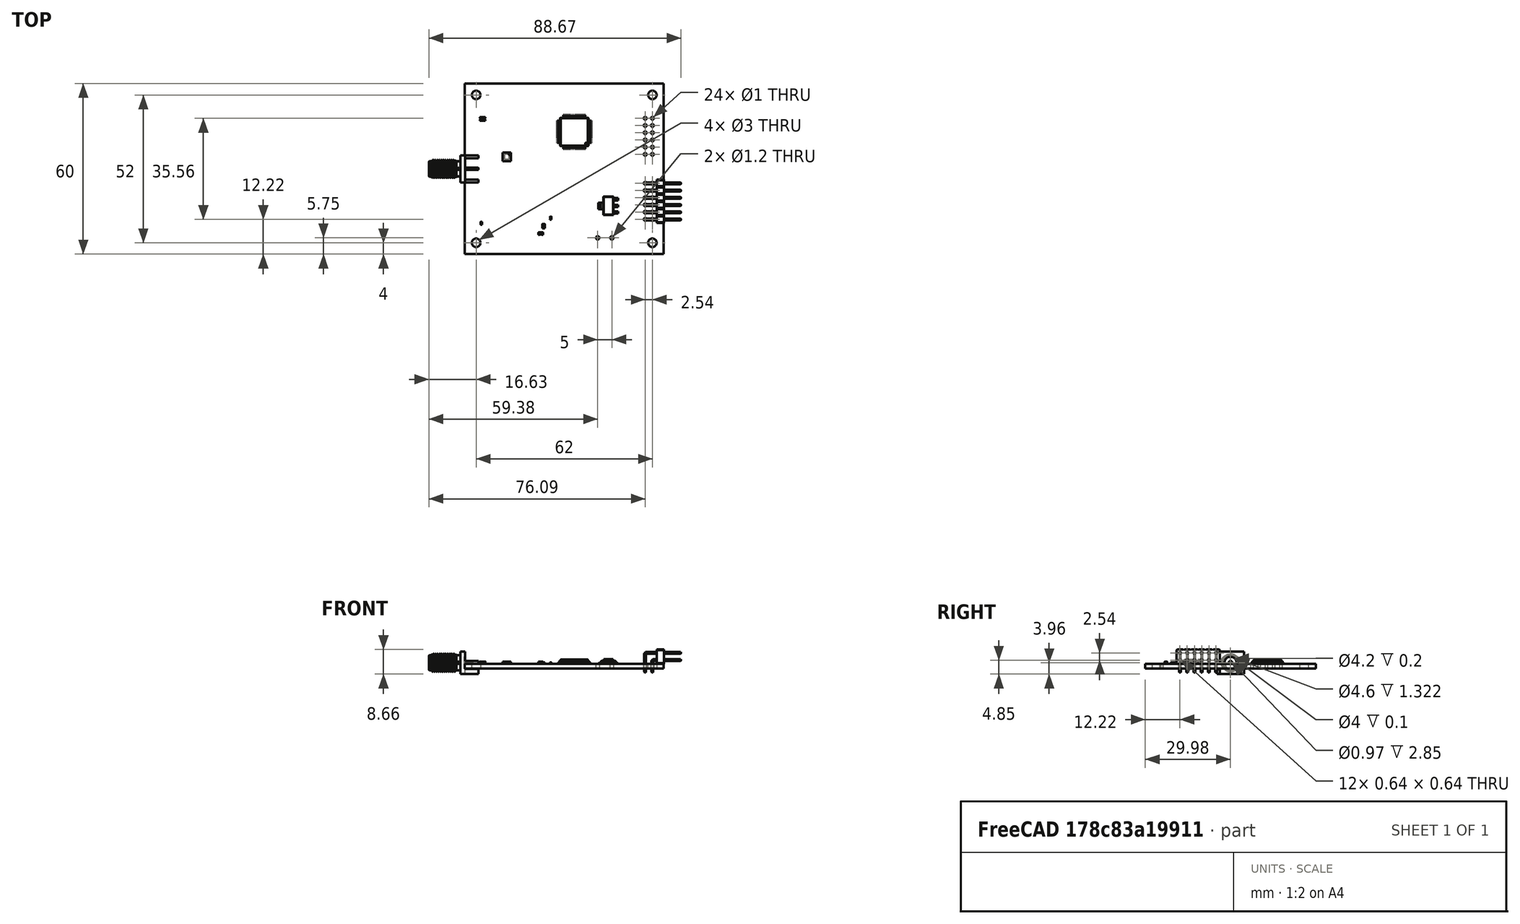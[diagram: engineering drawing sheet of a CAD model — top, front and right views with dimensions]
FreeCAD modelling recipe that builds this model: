
FCSTD DOCUMENT  (FreeCAD 1.0R39109 (Git))
Label: SixPort120_BDv2_12GHz
License: All rights reserved
LicenseURL: https://en.wikipedia.org/wiki/All_rights_reserved
objects: App::Link×60, Part::Feature×11, App::Part×4, PartDesign::CoordinateSystem×1, Sketcher::SketchObject×1
note: 14 computed .brp shape members not serialized (recipe doc carries the construction recipe); baked Part::Feature solids carry a one-line shape summary decoded from their .brp

FEATURE [PartDesign::CoordinateSystem] Local_CS_4f05
  AttacherType = Attacher::AttachEngine3D
  MapMode = 2
FEATURE [Part::Feature] Pcb_4f05
  Placement = pos=(-141,119.75,0) rot=(0,0,1;0rad)
  shape: bbox 70 x 60 x 1.6 mm, 36 faces (baked)
FEATURE [Sketcher::SketchObject] PCB_Sketch_4f05
  ArcFitTolerance = 1e-06
  FullyConstrained = false
  MakeInternals = false
  sketch-geometry (4):
    g0: LineSegment StartX=66 StartY=-4 StartZ=0 EndX=-4 EndY=-4 EndZ=0
    g1: LineSegment StartX=66 StartY=56 StartZ=0 EndX=66 EndY=-4 EndZ=0
    g2: LineSegment StartX=-4 StartY=56 StartZ=0 EndX=66 EndY=56 EndZ=0
    g3: LineSegment StartX=-4 StartY=-4 StartZ=0 EndX=-4 EndY=56 EndZ=0
  constraints (4):
    c: Coincident(g0,g3)
    c: Coincident(g2,g3)
    c: Coincident(g0,g1)
    c: Coincident(g1,g2)
FEATURE [App::Part] Board_Geoms_4f05
  Group = -> [Pcb_4f05,PCB_Sketch_4f05]
  Origin = -> Origin
FEATURE [Part::Feature] Shape  label="C2_1_C_0603_1608Metric_000061b49daf"
  Placement = pos=(22.7,3.25,0) rot=(0,0,1;3.14159rad)
  shape: bbox 1.6 x 0.8 x 0.8 mm, 28 faces (baked)
FEATURE [App::Link] C2_1_C_0603_1608Metric_000061b49daf_ln_  label="C2_2_1_C_0603_1608Metric_000061b49dc0"
  LinkPlacement = pos=(26,3.15,0) rot=(0,0,1;0rad)
  LinkedObject = -> Shape
  Placement = pos=(26,3.15,0) rot=(0,0,1;0rad)
FEATURE [App::Link] C2_1_C_0603_1608Metric_000061b49daf_ln_001  label="C2_3_1_C_0603_1608Metric_000061b49dd1"
  LinkPlacement = pos=(21.9,5.85,0) rot=(0,0,-1;1.5708rad)
  LinkedObject = -> Shape
  Placement = pos=(21.9,5.85,0) rot=(0,0,-1;1.5708rad)
FEATURE [Part::Feature] Shape001  label="C2_4_C_0402_1005Metric_000061b49de2"
  Placement = pos=(26.25,8.675,0) rot=(0,0,1;1.5708rad)
  shape: bbox 0.5 x 1 x 0.5 mm, 28 faces (baked)
FEATURE [App::Link] C2_4_C_0402_1005Metric_000061b49de2_ln_  label="C3_4_4_C_0402_1005Metric_000061b49df3"
  LinkPlacement = pos=(32.9,18.4,0) rot=(0,0,1;3.14159rad)
  LinkedObject = -> Shape001
  Placement = pos=(32.9,18.4,0) rot=(0,0,1;3.14159rad)
FEATURE [App::Link] C2_1_C_0603_1608Metric_000061b49daf_ln_002  label="C3_1_1_C_0603_1608Metric_000061b49e04"
  LinkPlacement = pos=(38.325,14.85,0) rot=(0,0,-1;1.5708rad)
  LinkedObject = -> Shape
  Placement = pos=(38.325,14.85,0) rot=(0,0,-1;1.5708rad)
FEATURE [App::Link] C2_1_C_0603_1608Metric_000061b49daf_ln_003  label="C3_2_1_C_0603_1608Metric_000061b49e15"
  LinkPlacement = pos=(38.425,18.15,0) rot=(0,0,1;1.5708rad)
  LinkedObject = -> Shape
  Placement = pos=(38.425,18.15,0) rot=(0,0,1;1.5708rad)
FEATURE [App::Link] C2_1_C_0603_1608Metric_000061b49daf_ln_004  label="C3_3_1_C_0603_1608Metric_000061b49e26"
  LinkPlacement = pos=(35.725,14.05,0) rot=(0,0,1;0rad)
  LinkedObject = -> Shape
  Placement = pos=(35.725,14.05,0) rot=(0,0,1;0rad)
FEATURE [App::Link] C2_1_C_0603_1608Metric_000061b49daf_ln_005  label="C4_1_1_C_0603_1608Metric_000061b49e37"
  LinkPlacement = pos=(33.7,29.8,0) rot=(0,0,1;0rad)
  LinkedObject = -> Shape
  Placement = pos=(33.7,29.8,0) rot=(0,0,1;0rad)
FEATURE [App::Link] C2_1_C_0603_1608Metric_000061b49daf_ln_006  label="C4_2_1_C_0603_1608Metric_000061b49e48"
  LinkPlacement = pos=(30.4,29.9,0) rot=(0,0,1;3.14159rad)
  LinkedObject = -> Shape
  Placement = pos=(30.4,29.9,0) rot=(0,0,1;3.14159rad)
FEATURE [App::Link] C2_1_C_0603_1608Metric_000061b49daf_ln_007  label="C4_3_1_C_0603_1608Metric_000061b49e59"
  LinkPlacement = pos=(34.6,27,0) rot=(0,0,1;1.5708rad)
  LinkedObject = -> Shape
  Placement = pos=(34.6,27,0) rot=(0,0,1;1.5708rad)
FEATURE [App::Link] C2_4_C_0402_1005Metric_000061b49de2_ln_001  label="C4_4_4_C_0402_1005Metric_000061b49e6a"
  LinkPlacement = pos=(30.15,24.38,0) rot=(0,0,-1;1.5708rad)
  LinkedObject = -> Shape001
  Placement = pos=(30.15,24.38,0) rot=(0,0,-1;1.5708rad)
FEATURE [App::Link] C2_1_C_0603_1608Metric_000061b49daf_ln_008  label="C5_1_1_C_0603_1608Metric_000061b49e7b"
  LinkPlacement = pos=(10.3,0.25,0) rot=(0,0,1;3.14159rad)
  LinkedObject = -> Shape
  Placement = pos=(10.3,0.25,0) rot=(0,0,1;3.14159rad)
FEATURE [App::Link] C2_1_C_0603_1608Metric_000061b49daf_ln_009  label="C5_2_1_C_0603_1608Metric_000061b49e8c"
  LinkPlacement = pos=(13.6,0.15,0) rot=(0,0,1;0rad)
  LinkedObject = -> Shape
  Placement = pos=(13.6,0.15,0) rot=(0,0,1;0rad)
FEATURE [App::Link] C2_1_C_0603_1608Metric_000061b49daf_ln_010  label="C5_3_1_C_0603_1608Metric_000061b49e9d"
  LinkPlacement = pos=(9.3,2.85,0) rot=(0,0,-1;1.5708rad)
  LinkedObject = -> Shape
  Placement = pos=(9.3,2.85,0) rot=(0,0,-1;1.5708rad)
FEATURE [App::Link] C2_4_C_0402_1005Metric_000061b49de2_ln_002  label="C5_4_4_C_0402_1005Metric_000061b49eae"
  LinkPlacement = pos=(13.75,5.675,0) rot=(0,0,1;1.5708rad)
  LinkedObject = -> Shape001
  Placement = pos=(13.75,5.675,0) rot=(0,0,1;1.5708rad)
FEATURE [Part::Feature] Shape002  label="R2_1_R_0603_1608Metric_000061b4a0a3"
  Placement = pos=(23.7,5.825,0) rot=(0,0,-1;1.5708rad)
  shape: bbox 0.8 x 1.6 x 0.45 mm, 26 faces (baked)
FEATURE [App::Link] R2_1_R_0603_1608Metric_000061b4a0a3_ln_  label="R3_1_1_R_0603_1608Metric_000061b4a0b4"
  LinkPlacement = pos=(35.725,15.85,0) rot=(0,0,1;0rad)
  LinkedObject = -> Shape002
  Placement = pos=(35.725,15.85,0) rot=(0,0,1;0rad)
FEATURE [App::Link] R2_1_R_0603_1608Metric_000061b4a0a3_ln_001  label="R4_1_1_R_0603_1608Metric_000061b4a0c5"
  LinkPlacement = pos=(32.7,27,0) rot=(0,0,1;1.5708rad)
  LinkedObject = -> Shape002
  Placement = pos=(32.7,27,0) rot=(0,0,1;1.5708rad)
FEATURE [App::Link] R2_1_R_0603_1608Metric_000061b4a0a3_ln_002  label="R5_1_1_R_0603_1608Metric_000061b4a0d6"
  LinkPlacement = pos=(11.1,2.85,0) rot=(0,0,-1;1.5708rad)
  LinkedObject = -> Shape002
  Placement = pos=(11.1,2.85,0) rot=(0,0,-1;1.5708rad)
FEATURE [Part::Feature] Shape003  label="R0_3_R_0402_1005Metric_000063accc0d"
  Placement = pos=(1.75,6.84,0) rot=(0,0,-1;1.5708rad)
  shape: bbox 0.5 x 1 x 0.35 mm, 26 faces (baked)
FEATURE [App::Link] R0_3_R_0402_1005Metric_000063accc0d_ln_  label="R0_2_3_R_0402_1005Metric_000063accc3d"
  LinkPlacement = pos=(9.48,10.29,0) rot=(0,0,1;3.14159rad)
  LinkedObject = -> Shape003
  Placement = pos=(9.48,10.29,0) rot=(0,0,1;3.14159rad)
FEATURE [App::Link] R0_3_R_0402_1005Metric_000063accc0d_ln_001  label="R0_1_3_R_0402_1005Metric_000063acccbe"
  LinkPlacement = pos=(9.48,18.4,0) rot=(0,0,1;3.14159rad)
  LinkedObject = -> Shape003
  Placement = pos=(9.48,18.4,0) rot=(0,0,1;3.14159rad)
FEATURE [App::Link] R0_3_R_0402_1005Metric_000063accc0d_ln_002  label="R0_4_3_R_0402_1005Metric_000063ad1704"
  LinkPlacement = pos=(5.54,6.84,0) rot=(0,0,-1;1.5708rad)
  LinkedObject = -> Shape003
  Placement = pos=(5.54,6.84,0) rot=(0,0,-1;1.5708rad)
FEATURE [App::Link] C2_1_C_0603_1608Metric_000061b49daf_ln_011  label="C7_1_1_C_0603_1608Metric_000063cef614"
  LinkPlacement = pos=(14.25,29.25,0) rot=(0,0,1;1.5708rad)
  LinkedObject = -> Shape
  Placement = pos=(14.25,29.25,0) rot=(0,0,1;1.5708rad)
FEATURE [App::Link] C2_1_C_0603_1608Metric_000061b49daf_ln_012  label="C7_3_1_C_0603_1608Metric_000063cef636"
  LinkPlacement = pos=(18.75,29.25,0) rot=(0,0,1;1.5708rad)
  LinkedObject = -> Shape
  Placement = pos=(18.75,29.25,0) rot=(0,0,1;1.5708rad)
FEATURE [App::Link] C2_1_C_0603_1608Metric_000061b49daf_ln_013  label="C7_4_1_C_0603_1608Metric_000063cef647"
  LinkPlacement = pos=(14.25,32.5,0) rot=(0,0,-1;1.5708rad)
  LinkedObject = -> Shape
  Placement = pos=(14.25,32.5,0) rot=(0,0,-1;1.5708rad)
FEATURE [App::Link] C2_1_C_0603_1608Metric_000061b49daf_ln_014  label="C7_5_1_C_0603_1608Metric_000063cef658"
  LinkPlacement = pos=(16.5,32.5,0) rot=(0,0,-1;1.5708rad)
  LinkedObject = -> Shape
  Placement = pos=(16.5,32.5,0) rot=(0,0,-1;1.5708rad)
FEATURE [App::Link] C2_1_C_0603_1608Metric_000061b49daf_ln_015  label="C7_6_1_C_0603_1608Metric_000063cef669"
  LinkPlacement = pos=(18.75,32.5,0) rot=(0,0,-1;1.5708rad)
  LinkedObject = -> Shape
  Placement = pos=(18.75,32.5,0) rot=(0,0,-1;1.5708rad)
FEATURE [App::Link] C2_1_C_0603_1608Metric_000061b49daf_ln_016  label="C8_1_1_C_0603_1608Metric_000063cef67a"
  LinkPlacement = pos=(46.5,8.25,0) rot=(0,0,1;0rad)
  LinkedObject = -> Shape
  Placement = pos=(46.5,8.25,0) rot=(0,0,1;0rad)
FEATURE [App::Link] C2_1_C_0603_1608Metric_000061b49daf_ln_017  label="C8_2_1_C_0603_1608Metric_000063cef68b"
  LinkPlacement = pos=(46.5,17.75,0) rot=(0,0,1;0rad)
  LinkedObject = -> Shape
  Placement = pos=(46.5,17.75,0) rot=(0,0,1;0rad)
FEATURE [App::Link] C2_1_C_0603_1608Metric_000061b49daf_ln_018  label="C8_3_1_C_0603_1608Metric_000063cef69c"
  LinkPlacement = pos=(46.5,20.5,0) rot=(0,0,1;0rad)
  LinkedObject = -> Shape
  Placement = pos=(46.5,20.5,0) rot=(0,0,1;0rad)
FEATURE [App::Link] C2_1_C_0603_1608Metric_000061b49daf_ln_019  label="C8_4_1_C_0603_1608Metric_000063cef6ad"
  LinkPlacement = pos=(47.25,30,0) rot=(0,0,1;0rad)
  LinkedObject = -> Shape
  Placement = pos=(47.25,30,0) rot=(0,0,1;0rad)
FEATURE [Part::Feature] Shape004  label="U7_1_QFN-12-1EP_3x3mm_Pitch0.5mm_000063cefc6c"
  Placement = pos=(10.75,30.25,0) rot=(0,0,-1;1.5708rad)
  shape: bbox 3 x 3 x 0.77 mm, 86 faces (baked)
FEATURE [Part::Feature] Shape005  label="U8_1_SOT_223_000063cefc82"
  Placement = pos=(46.5,13,0) rot=(0,0,1;3.14159rad)
  shape: bbox 7 x 6.5 x 1.7 mm, 78 faces (baked)
FEATURE [App::Link] U8_1_SOT_223_000063cefc82_ln_  label="U8_2_1_SOT_223_000063cefc98"
  LinkPlacement = pos=(46.5,25.25,0) rot=(0,0,1;3.14159rad)
  LinkedObject = -> Shape005
  Placement = pos=(46.5,25.25,0) rot=(0,0,1;3.14159rad)
FEATURE [App::Link] C2_1_C_0603_1608Metric_000061b49daf_ln_020  label="C7_2_1_C_0603_1608Metric_000063cf222f"
  LinkPlacement = pos=(16.5,29.25,0) rot=(0,0,1;1.5708rad)
  LinkedObject = -> Shape
  Placement = pos=(16.5,29.25,0) rot=(0,0,1;1.5708rad)
FEATURE [App::Link] C2_1_C_0603_1608Metric_000061b49daf_ln_021  label="C1_2_1_C_0603_1608Metric_000063d513af"
  LinkPlacement = pos=(11.5,44.75,0) rot=(0,0,1;1.5708rad)
  LinkedObject = -> Shape
  Placement = pos=(11.5,44.75,0) rot=(0,0,1;1.5708rad)
FEATURE [App::Link] C2_1_C_0603_1608Metric_000061b49daf_ln_022  label="C1_1_1_C_0603_1608Metric_000063d513bf"
  LinkPlacement = pos=(5.5,44.75,0) rot=(0,0,-1;1.5708rad)
  LinkedObject = -> Shape
  Placement = pos=(5.5,44.75,0) rot=(0,0,-1;1.5708rad)
FEATURE [App::Link] C2_1_C_0603_1608Metric_000061b49daf_ln_023  label="C1_15_1_C_0603_1608Metric_000063d513cf"
  LinkPlacement = pos=(16,37,0) rot=(0,0,1;0rad)
  LinkedObject = -> Shape
  Placement = pos=(16,37,0) rot=(0,0,1;0rad)
FEATURE [App::Link] C2_1_C_0603_1608Metric_000061b49daf_ln_024  label="C1_11_1_C_0603_1608Metric_000063d513df"
  LinkPlacement = pos=(15,44.75,0) rot=(0,0,1;1.5708rad)
  LinkedObject = -> Shape
  Placement = pos=(15,44.75,0) rot=(0,0,1;1.5708rad)
FEATURE [App::Link] C2_1_C_0603_1608Metric_000061b49daf_ln_025  label="C1_13_1_C_0603_1608Metric_000063d513ef"
  LinkPlacement = pos=(3.5,33.25,0) rot=(0,0,1;3.14159rad)
  LinkedObject = -> Shape
  Placement = pos=(3.5,33.25,0) rot=(0,0,1;3.14159rad)
FEATURE [App::Link] C2_1_C_0603_1608Metric_000061b49daf_ln_026  label="C1_9_1_C_0603_1608Metric_000063d513ff"
  LinkPlacement = pos=(16.75,44.75,0) rot=(0,0,1;1.5708rad)
  LinkedObject = -> Shape
  Placement = pos=(16.75,44.75,0) rot=(0,0,1;1.5708rad)
FEATURE [App::Link] C2_1_C_0603_1608Metric_000061b49daf_ln_027  label="C1_8_1_C_0603_1608Metric_000063d5140f"
  LinkPlacement = pos=(16,42.25,0) rot=(0,0,1;0rad)
  LinkedObject = -> Shape
  Placement = pos=(16,42.25,0) rot=(0,0,1;0rad)
FEATURE [App::Link] C2_1_C_0603_1608Metric_000061b49daf_ln_028  label="C1_10_1_C_0603_1608Metric_000063d5141f"
  LinkPlacement = pos=(13.25,44.75,0) rot=(0,0,1;1.5708rad)
  LinkedObject = -> Shape
  Placement = pos=(13.25,44.75,0) rot=(0,0,1;1.5708rad)
FEATURE [App::Link] C2_1_C_0603_1608Metric_000061b49daf_ln_029  label="C1_5_1_C_0603_1608Metric_000063d5144f"
  LinkPlacement = pos=(3.5,35,0) rot=(0,0,1;3.14159rad)
  LinkedObject = -> Shape
  Placement = pos=(3.5,35,0) rot=(0,0,1;3.14159rad)
FEATURE [App::Link] C2_1_C_0603_1608Metric_000061b49daf_ln_030  label="C1_3_1_C_0603_1608Metric_000063d5145f"
  LinkPlacement = pos=(3.5,41.5,0) rot=(0,0,1;3.14159rad)
  LinkedObject = -> Shape
  Placement = pos=(3.5,41.5,0) rot=(0,0,1;3.14159rad)
FEATURE [App::Link] C2_1_C_0603_1608Metric_000061b49daf_ln_031  label="C1_14_1_C_0603_1608Metric_000063d5146f"
  LinkPlacement = pos=(3.5,31.5,0) rot=(0,0,1;3.14159rad)
  LinkedObject = -> Shape
  Placement = pos=(3.5,31.5,0) rot=(0,0,1;3.14159rad)
FEATURE [App::Link] C2_1_C_0603_1608Metric_000061b49daf_ln_032  label="C1_4_1_C_0603_1608Metric_000063d5147f"
  LinkPlacement = pos=(3.5,38.5,0) rot=(0,0,1;3.14159rad)
  LinkedObject = -> Shape
  Placement = pos=(3.5,38.5,0) rot=(0,0,1;3.14159rad)
FEATURE [App::Link] C2_4_C_0402_1005Metric_000061b49de2_ln_003  label="C1_12_4_C_0402_1005Metric_000063d514e4"
  LinkPlacement = pos=(10.75,34.15,0) rot=(0,0,1;1.5708rad)
  LinkedObject = -> Shape001
  Placement = pos=(10.75,34.15,0) rot=(0,0,1;1.5708rad)
FEATURE [App::Link] R2_1_R_0603_1608Metric_000061b4a0a3_ln_003  label="R1_3_1_R_0603_1608Metric_000063d51504"
  LinkPlacement = pos=(1,32.25,0) rot=(0,0,1;1.5708rad)
  LinkedObject = -> Shape002
  Placement = pos=(1,32.25,0) rot=(0,0,1;1.5708rad)
FEATURE [Part::Feature] Shape006  label="D1_1_D_0805_000063d51534"
  Placement = pos=(2.25,43.5,0) rot=(0,0,1;3.14159rad)
  shape: bbox 2 x 1.27 x 0.8 mm, 39 faces (baked)
FEATURE [App::Link] R2_1_R_0603_1608Metric_000061b4a0a3_ln_004  label="R1_1_1_R_0603_1608Metric_000063d5338b"
  LinkPlacement = pos=(2.75,45.5,0) rot=(0,0,1;0rad)
  LinkedObject = -> Shape002
  Placement = pos=(2.75,45.5,0) rot=(0,0,1;0rad)
FEATURE [App::Link] R2_1_R_0603_1608Metric_000061b4a0a3_ln_005  label="R1_5_1_R_0603_1608Metric_000063d53636"
  LinkPlacement = pos=(16,40.5,0) rot=(0,0,1;0rad)
  LinkedObject = -> Shape002
  Placement = pos=(16,40.5,0) rot=(0,0,1;0rad)
FEATURE [App::Link] R2_1_R_0603_1608Metric_000061b4a0a3_ln_006  label="R1_2_1_R_0603_1608Metric_000063d54fa1"
  LinkPlacement = pos=(16,38.75,0) rot=(0,0,1;3.14159rad)
  LinkedObject = -> Shape002
  Placement = pos=(16,38.75,0) rot=(0,0,1;3.14159rad)
FEATURE [App::Link] C2_1_C_0603_1608Metric_000061b49daf_ln_033  label="C1_6_1_C_0603_1608Metric_000063d56b6d"
  LinkPlacement = pos=(19.25,35,0) rot=(0,0,1;0rad)
  LinkedObject = -> Shape
  Placement = pos=(19.25,35,0) rot=(0,0,1;0rad)
FEATURE [App::Link] C2_1_C_0603_1608Metric_000061b49daf_ln_034  label="C1_7_1_C_0603_1608Metric_000063d56b9f"
  LinkPlacement = pos=(16,35,0) rot=(0,0,1;3.14159rad)
  LinkedObject = -> Shape
  Placement = pos=(16,35,0) rot=(0,0,1;3.14159rad)
FEATURE [App::Link] C2_1_C_0603_1608Metric_000061b49daf_ln_035  label="C6_2_1_C_0603_1608Metric_000063d66c4c"
  LinkPlacement = pos=(25.25,40.75,0) rot=(0,0,1;3.14159rad)
  LinkedObject = -> Shape
  Placement = pos=(25.25,40.75,0) rot=(0,0,1;3.14159rad)
FEATURE [App::Link] C2_1_C_0603_1608Metric_000061b49daf_ln_036  label="C6_9_1_C_0603_1608Metric_000063d66c5c"
  LinkPlacement = pos=(25.25,44.25,0) rot=(0,0,1;3.14159rad)
  LinkedObject = -> Shape
  Placement = pos=(25.25,44.25,0) rot=(0,0,1;3.14159rad)
FEATURE [App::Link] C2_1_C_0603_1608Metric_000061b49daf_ln_037  label="C6_5_1_C_0603_1608Metric_000063d66c6c"
  LinkPlacement = pos=(25.25,42.5,0) rot=(0,0,1;3.14159rad)
  LinkedObject = -> Shape
  Placement = pos=(25.25,42.5,0) rot=(0,0,1;3.14159rad)
FEATURE [App::Link] C2_1_C_0603_1608Metric_000061b49daf_ln_038  label="C6_4_1_C_0603_1608Metric_000063d66c7c"
  LinkPlacement = pos=(25.25,37.25,0) rot=(0,0,1;3.14159rad)
  LinkedObject = -> Shape
  Placement = pos=(25.25,37.25,0) rot=(0,0,1;3.14159rad)
FEATURE [App::Link] C2_1_C_0603_1608Metric_000061b49daf_ln_039  label="C6_8_1_C_0603_1608Metric_000063d66c8c"
  LinkPlacement = pos=(42.5,37.5,0) rot=(0,0,-1;1.5708rad)
  LinkedObject = -> Shape
  Placement = pos=(42.5,37.5,0) rot=(0,0,-1;1.5708rad)
FEATURE [App::Link] C2_1_C_0603_1608Metric_000061b49daf_ln_040  label="C6_6_1_C_0603_1608Metric_000063d66c9c"
  LinkPlacement = pos=(25.25,39,0) rot=(0,0,1;3.14159rad)
  LinkedObject = -> Shape
  Placement = pos=(25.25,39,0) rot=(0,0,1;3.14159rad)
FEATURE [Part::Feature] Shape007  label="U6_1_LQFP_64_10x10mm_P05mm_000063d66cac"
  Placement = pos=(34.5,39,0) rot=(0,0,1;3.14159rad)
  shape: bbox 12 x 12 x 1.5 mm, 1004 faces (baked)
FEATURE [App::Link] C2_1_C_0603_1608Metric_000061b49daf_ln_041  label="C6_7_1_C_0603_1608Metric_000063d66d16"
  LinkPlacement = pos=(25.25,35.5,0) rot=(0,0,1;3.14159rad)
  LinkedObject = -> Shape
  Placement = pos=(25.25,35.5,0) rot=(0,0,1;3.14159rad)
FEATURE [App::Link] C2_1_C_0603_1608Metric_000061b49daf_ln_042  label="C6_3_1_C_0603_1608Metric_000063d66d26"
  LinkPlacement = pos=(25.25,33.75,0) rot=(0,0,1;3.14159rad)
  LinkedObject = -> Shape
  Placement = pos=(25.25,33.75,0) rot=(0,0,1;3.14159rad)
FEATURE [App::Link] C2_1_C_0603_1608Metric_000061b49daf_ln_043  label="C6_1_1_C_0603_1608Metric_000063d66d87"
  LinkPlacement = pos=(42.5,34.3,0) rot=(0,0,-1;1.5708rad)
  LinkedObject = -> Shape
  Placement = pos=(42.5,34.3,0) rot=(0,0,-1;1.5708rad)
FEATURE [Part::Feature] Shape008  label="J4_PinHeader_2x06_P254mm_Horizontal_000063d8358e"
  Placement = pos=(59.46,20.92,0) rot=(0,0,1;0rad)
  shape: bbox 12.9 x 15.24 x 8.08 mm, 292 faces (baked)
FEATURE [App::Link] J4_PinHeader_2x06_P254mm_Horizontal_000063d8358e_ln_  label="J3_PinHeader_2x06_P254mm_Horizontal_000063d869aa"
  LinkPlacement = pos=(59.46,43.78,0) rot=(0,0,1;0rad)
  LinkedObject = -> Shape008
  Placement = pos=(59.46,43.78,0) rot=(0,0,1;0rad)
FEATURE [Part::Feature] Shape009  label="J1_SMA_Amphenol_132289_EdgeMount_000063d959b3"
  Placement = pos=(-1.39,25.98,0) rot=(0,0,1;3.14159rad)
  shape: bbox 17.53 x 11.27 x 10.81 mm, 111 faces (baked)
FEATURE [App::Part] Top_4f05
  Group = -> [Shape,C2_1_C_0603_1608Metric_000061b49daf_ln_,C2_1_C_0603_1608Metric_000061b49daf_ln_001,Shape001,C2_4_C_0402_1005Metric_000061b49de2_ln_,C2_1_C_0603_1608Metric_000061b49daf_ln_002,C2_1_C_0603_1608Metric_000061b49daf_ln_003,C2_1_C_0603_1608Metric_000061b49daf_ln_004,C2_1_C_0603_1608Metric_000061b49daf_ln_005,C2_1_C_0603_1608Metric_000061b49daf_ln_006,C2_1_C_0603_1608Metric_000061b49daf_ln_007,+59 more]
  Origin = -> Origin003
FEATURE [App::Part] Step_Models_4f05
  Group = -> [Top_4f05]
  Origin = -> Origin002
FEATURE [App::Part] Board_4f05  label="SixPort120_BDv2_12GHz"
  Group = -> [Local_CS_4f05,Board_Geoms_4f05,Step_Models_4f05]
  Origin = -> Origin001
